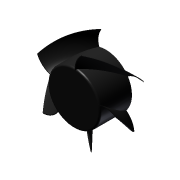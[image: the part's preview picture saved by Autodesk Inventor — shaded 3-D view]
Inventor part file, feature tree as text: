
AUTODESK INVENTOR PART (.ipt)
format: ipt  version: 2013 (Build 170138000, 138)  size: 238,592 bytes
history: native  units: mm (DEFAULTED — no unit token found)
features: sketch x2, extrude x1, fillet x1, other x1, helix x1, pattern_circular x1
ambient origin geometry x8: Origin, YZ Plane, XZ Plane, XY Plane, X Axis, Y Axis, Z Axis, Center Point
bodies: Solid1 (feature_tree)
feature tree (7):
  extrude  "Extrusion1"  Depth=0.79375mm
  fillet  "Fillet1"  Radius=0.3175mm
  sketch  "Sketch2"  dims[d5=0.698132mm d6=8.89mm d7=37.338mm d8=127.0mm d9=14.3002mm d10=1.5mm d11=0.0mm d12=90.0deg d13=90.0deg d14=0.0mm d15=0.0mm d16=50.0mm d18=360.0deg]
  other  "Work Axis1"
  helix  "Coil1"  [1 undecoded]
  pattern_circular  "Circular Pattern1"  [2 undecoded]
  sketch  "Sketch1"  dims[d0=14.3002mm d1=0.0mm d2=0.79375mm d3=0.3175mm d4=2.094086mm]
note: 3 required parameter values undecoded (feature->parameter linkage not recoverable at this tier; creation-order binding heuristic only, values carry confidence <= 0.55)
